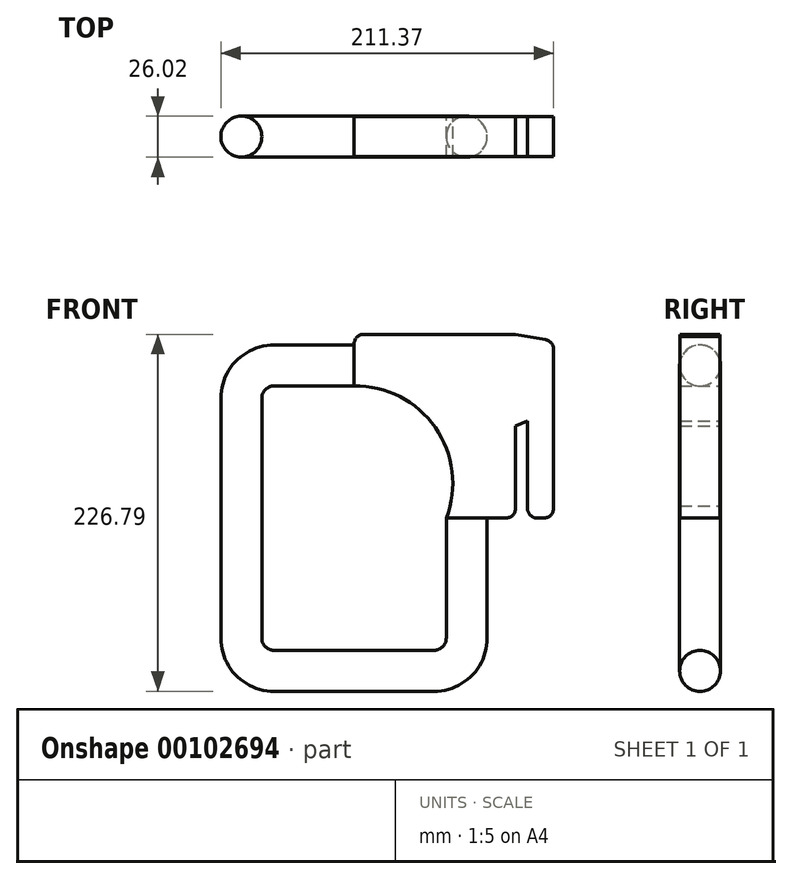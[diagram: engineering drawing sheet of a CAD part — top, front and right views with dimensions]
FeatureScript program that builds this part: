
annotation { "Feature Type Name" : "Feature", "Feature Type Description" : "" }
export const myFeature = defineFeature(function(context is Context, id is Id, definition is map)
    precondition{}
    {
        {
            var Q0;
            Q0=qCreatedBy(makeId("Front.planeOp"),FACE);
            var sketch = newSketch(context, id + "F0", { "sketchPlane" : qUnion([Q0])});
            skLineSegment(sketch, "E0", {"start": v(0, 96.97) * mm, "end": v(-50.8, 96.97) * mm});
            skArc(sketch, "E1", {"start": v(-50.8, 96.97) * mm, "mid": v(-65.49, 90.89) * mm, "end": v(-71.57, 76.2) * mm});
            skLineSegment(sketch, "E2", {"start": v(-50.8, 76.2) * mm, "end": v(-50.8, 96.97) * mm, "construction": true});
            skLineSegment(sketch, "E3", {"start": v(-50.8, 76.2) * mm, "end": v(-71.57, 76.2) * mm, "construction": true});
            skLineSegment(sketch, "E4.bottom", {"start": v(-71.57, 34.8) * mm, "end": v(71.57, 34.8) * mm, "construction": true});
            skLineSegment(sketch, "E4.top", {"start": v(-71.57, -34.8) * mm, "end": v(71.57, -34.8) * mm, "construction": true});
            skLineSegment(sketch, "E4.left", {"start": v(-71.57, 34.8) * mm, "end": v(-71.57, 0) * mm, "construction": true});
            skLineSegment(sketch, "E4.right", {"start": v(71.57, 34.8) * mm, "end": v(71.57, -34.8) * mm, "construction": true});
            skLineSegment(sketch, "E5", {"start": v(-71.57, 34.8) * mm, "end": v(0, 0) * mm, "construction": true});
            skLineSegment(sketch, "E6", {"start": v(71.57, 34.8) * mm, "end": v(-71.57, -34.8) * mm, "construction": true});
            skLineSegment(sketch, "E7", {"start": v(0, 0) * mm, "end": v(71.57, -34.8) * mm, "construction": true});
            skLineSegment(sketch, "E8", {"start": v(-71.57, 0) * mm, "end": v(-71.57, -34.8) * mm, "construction": true});
            skLineSegment(sketch, "E9", {"start": v(-71.57, 76.2) * mm, "end": v(-71.57, 0) * mm});
            skLineSegment(sketch, "E10.MirrorCS", {"start": v(0, -96.97) * mm, "end": v(-50.8, -96.97) * mm});
            skLineSegment(sketch, "E11.MirrorCS", {"start": v(-50.8, -76.2) * mm, "end": v(-50.8, -96.97) * mm, "construction": true});
            skLineSegment(sketch, "E12.MirrorCS", {"start": v(-71.57, -76.2) * mm, "end": v(-71.57, 0) * mm});
            skLineSegment(sketch, "E13.MirrorCS", {"start": v(-50.8, -76.2) * mm, "end": v(-71.57, -76.2) * mm, "construction": true});
            skArc(sketch, "E14.MirrorCS", {"start": v(-50.8, -96.97) * mm, "mid": v(-65.49, -90.89) * mm, "end": v(-71.57, -76.2) * mm});
            skLineSegment(sketch, "E15.MirrorCS", {"start": v(50.8, -76.2) * mm, "end": v(50.8, -96.97) * mm, "construction": true});
            skLineSegment(sketch, "E16.MirrorCS", {"start": v(50.8, -76.2) * mm, "end": v(71.57, -76.2) * mm, "construction": true});
            skLineSegment(sketch, "E17.MirrorCS", {"start": v(0, -96.97) * mm, "end": v(50.8, -96.97) * mm});
            skArc(sketch, "E18.MirrorCS", {"start": v(50.8, -96.97) * mm, "mid": v(65.49, -90.89) * mm, "end": v(71.57, -76.2) * mm});
            skLineSegment(sketch, "E19.MirrorCS", {"start": v(71.57, -76.2) * mm, "end": v(71.57, 0) * mm});
            skSolve(sketch);
        }
        {
            var Q0;
            Q0=qCreatedBy(makeId("Right.planeOp"),FACE);
            var sketch = newSketch(context, id + "F1", { "sketchPlane" : qUnion([Q0])});
            skCircle(sketch, "E20", {"center": v(0, 96.97) * mm, "radius": 13 * mm});
            skSolve(sketch);
        }
        {
            var Q0;
            Q0=makeQuery(id+"F1.imprint","IMPRINT",FACE,{"disambiguationData":[TD([[makeQuery(id+"F1.imprint","IMPRINT",EDGE,{"derivedFrom":sQuery(id+"F1.wireOp",EDGE,"E20")}),1.0]])]});
            var Q1;
            Q1=sQuery(id+"F0.wireOp",EDGE,"E0");
            var Q2;
            Q2=sQuery(id+"F0.wireOp",EDGE,"E1");
            var Q3;
            Q3=sQuery(id+"F0.wireOp",EDGE,"E9");
            var Q4;
            Q4=sQuery(id+"F0.wireOp",EDGE,"E12.MirrorCS");
            var Q5;
            Q5=sQuery(id+"F0.wireOp",EDGE,"E14.MirrorCS");
            var Q6;
            Q6=sQuery(id+"F0.wireOp",EDGE,"E10.MirrorCS");
            var Q7;
            Q7=sQuery(id+"F0.wireOp",EDGE,"E17.MirrorCS");
            var Q8;
            Q8=sQuery(id+"F0.wireOp",EDGE,"E18.MirrorCS");
            var Q9;
            Q9=sQuery(id+"F0.wireOp",EDGE,"E19.MirrorCS");
            sweep(context, id + "F2", {"profiles" : qUnion([Q0]), "path" : qUnion([Q1, Q2, Q3, Q4, Q5, Q6, Q7, Q8, Q9])});
        }
        {
            var Q0;
            Q0=qCreatedBy(makeId("Front.planeOp"),FACE);
            var sketch = newSketch(context, id + "F3", { "sketchPlane" : qUnion([Q0])});
            skLineSegment(sketch, "E21.bottom", {"start": v(102.66, 116.81) * mm, "end": v(110.28, 115.5) * mm});
            skLineSegment(sketch, "E22", {"start": v(110.28, 115.5) * mm, "end": v(121.6, 113.4) * mm});
            skLineSegment(sketch, "E23.top", {"start": v(116.5, 0) * mm, "end": v(120.44, 0) * mm});
            skLineSegment(sketch, "E24.bottom", {"start": v(102.66, 116.81) * mm, "end": v(51.33, 116.81) * mm});
            skLineSegment(sketch, "E24.top", {"start": v(96.31, 0) * mm, "end": v(58.57, 0) * mm});
            skLineSegment(sketch, "E24.left", {"start": v(102.66, 116.81) * mm, "end": v(102.66, 58.4) * mm});
            skLineSegment(sketch, "E24.right", {"start": v(0, 110.46) * mm, "end": v(0, 83.97) * mm});
            skLineSegment(sketch, "E25.0", {"start": v(0, 83.97) * mm, "end": v(0, 109.98) * mm});
            skLineSegment(sketch, "E26.0", {"start": v(58.57, 0) * mm, "end": v(84.58, 0) * mm});
            skArc(sketch, "E27", {"start": v(58.57, 0) * mm, "mid": v(51.64, 57.58) * mm, "end": v(0, 83.97) * mm});
            skLineSegment(sketch, "E28", {"start": v(51.33, 116.81) * mm, "end": v(6.35, 116.81) * mm});
            skPoint(sketch, "E29.visualSharp", {"position": v(103.21, 0) * mm});
            skArc(sketch, "E29.filletArc", {"start": v(110.28, 7.67) * mm, "mid": v(111.56, 2.35) * mm, "end": v(116.5, 0) * mm});
            skLineSegment(sketch, "E30", {"start": v(110.28, 115.5) * mm, "end": v(110.28, 61.58) * mm});
            skLineSegment(sketch, "E31", {"start": v(126.8, 6.35) * mm, "end": v(126.8, 61.58) * mm});
            skLineSegment(sketch, "E32", {"start": v(110.28, 61.58) * mm, "end": v(110.28, 7.67) * mm});
            skLineSegment(sketch, "E33", {"start": v(102.66, 58.4) * mm, "end": v(102.66, 6.35) * mm});
            skLineSegment(sketch, "E34", {"start": v(110.28, 61.58) * mm, "end": v(102.66, 58.4) * mm});
            skPoint(sketch, "E35.visualSharp", {"position": v(0, 116.81) * mm});
            skArc(sketch, "E35.filletArc", {"start": v(6.35, 116.81) * mm, "mid": v(1.86, 114.95) * mm, "end": v(0, 110.46) * mm});
            skPoint(sketch, "E36.visualSharp", {"position": v(102.66, 0) * mm});
            skArc(sketch, "E36.filletArc", {"start": v(96.31, 0) * mm, "mid": v(100.8, 1.86) * mm, "end": v(102.66, 6.35) * mm});
            skPoint(sketch, "E37.visualSharp", {"position": v(126.8, 0) * mm});
            skArc(sketch, "E37.filletArc", {"start": v(120.44, 0) * mm, "mid": v(124.94, 1.86) * mm, "end": v(126.8, 6.35) * mm});
            skPoint(sketch, "E38.visualSharp", {"position": v(126.8, 112.43) * mm});
            skArc(sketch, "E38.filletArc", {"start": v(126.8, 107.15) * mm, "mid": v(125.33, 111.2) * mm, "end": v(121.6, 113.4) * mm});
            skLineSegment(sketch, "E39", {"start": v(126.8, 61.58) * mm, "end": v(126.8, 107.15) * mm});
            skLineSegment(sketch, "E40", {"start": v(110.28, 61.58) * mm, "end": v(126.8, 61.58) * mm});
            skSolve(sketch);
        }
        {
            var Q0;
            Q0 = qSketchRegion(id + "F3", true);
            extrude(context, id + "F4", {"entities" : qUnion([Q0]), "endBound" : BoundingType.SYMMETRIC, "depth" : 25.4 * mm});
        }
    });
